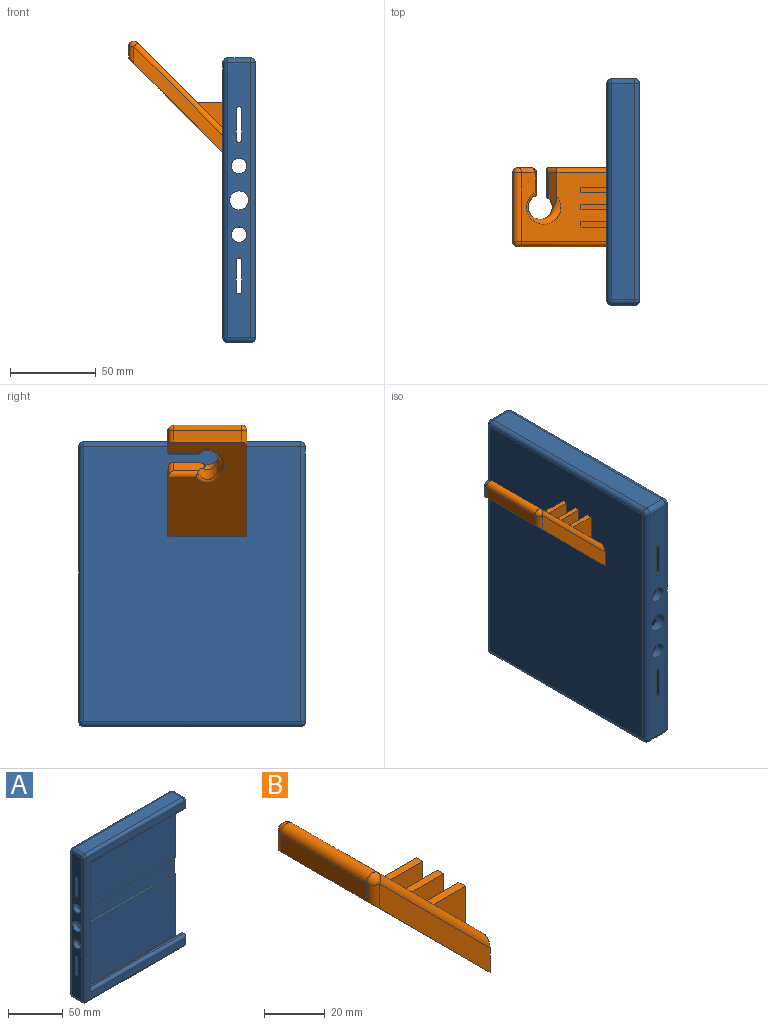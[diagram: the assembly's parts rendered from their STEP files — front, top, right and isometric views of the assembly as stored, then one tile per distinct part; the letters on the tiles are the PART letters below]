
ASSEMBLY  parts=2 mates=1
PART A: 63 faces, bbox 132x19x166 mm
  f0: plane 10x6.5mm, normal (1,0,0), area 25.9mm2, adj f23,f35,f36,f37,f54,f59
  f1: plane 71x6.5mm, normal (1,0,0), area 147.9mm2, adj f32,f33,f34,f35,f44,f54
  f2: plane 10x6.5mm, normal (1,0,0), area 25.9mm2, adj f24,f25,f26,f27,f53,f58
  f3: plane 40x11mm, normal (1,0,0), area 241.6mm2, adj f16,f17,f18,f25,f29,f30,f31,f32
  f4: plane 60x9mm, normal (1,0,0), area 435.4mm2, adj f6,f7,f8,f17,f20,f33,f34,f35
  f5: plane 60x9mm, normal (1,0,0), area 435.4mm2, adj f9,f10,f11,f15,f18,f25,f26,f27
  f6: cylinder r=1.5mm len=5mm, axis (1,0,0), area 23.6mm2, adj f4,f7,f20,f21
  f7: plane 18x5mm, normal (0,1,0), area 90mm2, adj f4,f6,f8,f21
  f8: cylinder r=1.5mm len=5mm, axis (1,0,0), area 23.6mm2, adj f4,f7,f20,f21
  f9: cylinder r=1.5mm len=5mm, axis (1,0,0), area 23.6mm2, adj f5,f10,f15,f21
  f10: plane 18x5mm, normal (0,-1,0), area 90mm2, adj f5,f9,f11,f21
  f11: cylinder r=1.5mm len=5mm, axis (1,0,0), area 23.6mm2, adj f5,f10,f15,f21
  f12: plane 126x13mm, normal (0,0,1), area 1638mm2, adj f42,f43,f52,f53
  f13: plane 160x126mm, normal (0,-1,0), area 2348mm2, adj f47,f52,f55,f58,f59,f60,f61,f62
  f14: plane 126x13mm, normal (0,0,-1), area 1638mm2, adj f45,f46,f54,f55
  f15: plane 18x5mm, normal (0,1,0), area 90mm2, adj f5,f9,f11,f21
  f16: cylinder r=5.5mm len=11mm, axis (1,0,0), area 206.5mm2, adj f3,f21,f25,f36,f38
  f17: cylinder r=4.5mm len=9mm, axis (1,0,0), area 141.4mm2, adj f3,f4,f21
  f18: cylinder r=4.5mm len=9mm, axis (1,0,0), area 141.4mm2, adj f3,f5,f21
  f19: plane 160x126mm, normal (0,1,0), area 20160mm2, adj f39,f43,f44,f45
  f20: plane 18x5mm, normal (0,-1,0), area 90mm2, adj f4,f6,f8,f21
  f21: plane 160x13mm, normal (-1,0,0), area 1735.6mm2, adj f6,f7,f8,f9,f10,f11,f15,f16
  f22: plane 71x6.5mm, normal (1,0,0), area 147.9mm2, adj f27,f28,f29,f30,f44,f53
  f23: plane 122x2mm, normal (0,0,1), area 244mm2, adj f0,f36,f38,f61
  f24: plane 122x2mm, normal (0,0,-1), area 244mm2, adj f2,f25,f38,f60
  f25: plane 127x74.84mm, normal (0,1,0), area 1350.2mm2, adj f2,f3,f5,f16,f24,f26,f38
  f26: plane 127x2.5mm, normal (0,0,-1), area 317.5mm2, adj f2,f5,f25,f27
  f27: cylinder r=2mm len=127mm, axis (-1,0,0), area 798mm2, adj f2,f5,f22,f26,f28
  f28: plane 127x2.5mm, normal (0,0,-1), area 317.5mm2, adj f5,f22,f27,f29
  f29: plane 127x69mm, normal (0,-1,0), area 8763mm2, adj f3,f5,f22,f28,f30
  f30: plane 127x2mm, normal (0,0,-1), area 254mm2, adj f3,f22,f29,f31
  f31: plane 127x18mm, normal (0,-1,0), area 2286mm2, adj f3,f30,f32,f44
  f32: plane 127x2mm, normal (0,0,1), area 254mm2, adj f1,f3,f31,f33
  f33: plane 127x69mm, normal (0,-1,0), area 8763mm2, adj f1,f3,f4,f32,f34
  f34: plane 127x2.5mm, normal (0,0,1), area 317.5mm2, adj f1,f4,f33,f35
  f35: cylinder r=2mm len=127mm, axis (-1,0,0), area 798mm2, adj f0,f1,f4,f34,f37
  f36: plane 127x74.84mm, normal (0,1,0), area 1350.2mm2, adj f0,f3,f4,f16,f23,f37,f38
  f37: plane 127x2.5mm, normal (0,0,1), area 317.5mm2, adj f0,f4,f35,f36
  f38: plane 140x2mm, normal (1,0,0), area 275.7mm2, adj f16,f23,f24,f25,f36,f62
  f39: cylinder r=3mm len=160mm, axis (0,0,-1), area 754mm2, adj f19,f21,f40,f41
  f40: sphere r=3mm, area 14.1mm2, adj f39,f42,f43
  f41: sphere r=3mm, area 14.1mm2, adj f39,f45,f46
  f42: cylinder r=3mm len=13mm, axis (0,1,0), area 61.3mm2, adj f12,f21,f40,f48
  f43: cylinder r=3mm len=126mm, axis (1,0,0), area 593.8mm2, adj f12,f19,f40,f49
  f44: cylinder r=3mm len=160mm, axis (0,0,1), area 754mm2, adj f1,f19,f22,f31,f49,f50
  f45: cylinder r=3mm len=126mm, axis (-1,0,0), area 593.8mm2, adj f14,f19,f41,f50
  f46: cylinder r=3mm len=13mm, axis (0,-1,0), area 61.3mm2, adj f14,f21,f41,f51
  f47: cylinder r=3mm len=160mm, axis (0,0,1), area 754mm2, adj f13,f21,f48,f51
  f48: sphere r=3mm, area 14.1mm2, adj f42,f47,f52
  f49: sphere r=3mm, area 14.1mm2, adj f43,f44,f53
  f50: sphere r=3mm, area 14.1mm2, adj f44,f45,f54
  f51: sphere r=3mm, area 14.1mm2, adj f46,f47,f55
  f52: cylinder r=3mm len=126mm, axis (-1,0,0), area 593.8mm2, adj f12,f13,f48,f56
  f53: cylinder r=3mm len=13mm, axis (0,-1,0), area 61.3mm2, adj f2,f12,f22,f49,f56
  f54: cylinder r=3mm len=13mm, axis (0,1,0), area 61.3mm2, adj f0,f1,f14,f50,f57
  f55: cylinder r=3mm len=126mm, axis (1,0,0), area 593.8mm2, adj f13,f14,f51,f57
  f56: sphere r=3mm, area 14.1mm2, adj f52,f53,f58
  f57: sphere r=3mm, area 14.1mm2, adj f54,f55,f59
  f58: cylinder r=3mm len=10mm, axis (0,0,-1), area 42mm2, adj f2,f13,f56,f60
  f59: cylinder r=3mm len=10mm, axis (0,0,-1), area 42mm2, adj f0,f13,f57,f61
  f60: cylinder r=3mm len=125mm, axis (1,0,0), area 574.9mm2, adj f13,f24,f58,f62
  f61: cylinder r=3mm len=125mm, axis (1,0,0), area 574.9mm2, adj f13,f23,f59,f62
  f62: cylinder r=3mm len=146mm, axis (0,0,-1), area 670mm2, adj f13,f38,f60,f61
PART B: 35 faces, bbox 58.2x47.3x66 mm
  f0: plane 49.7x49.7mm, normal (0.71,0,0.71), area 1981mm2, adj f3,f9,f10,f13,f15,f17,f18,f25
  f1: plane 38.89x33.94mm, normal (0,1,0), area 311.5mm2, adj f3,f4,f24,f25
  f2: plane 40x6.9mm, normal (-1,0,0), area 276mm2, adj f4,f11,f13,f14
  f3: plane 47.26x30.4mm, normal (1,0,0), area 780.1mm2, adj f0,f1,f4,f6,f10,f25,f26,f27
  f4: plane 56.08x56.08mm, normal (-0.71,0,-0.71), area 2821.9mm2, adj f1,f2,f3,f5,f6,f11,f14,f21
  f5: plane 12.93x7.98mm, normal (0,1,0), area 54.5mm2, adj f4,f14,f18,f20
  f6: plane 61.72x51.82mm, normal (0,-1,0), area 513mm2, adj f3,f4,f10,f11
  f7: cylinder r=7mm len=25.77mm, axis (0,0,-1), area 193.6mm2, adj f8,f9,f15,f17,f22,f23
  f8: plane 15.39x2.96mm, normal (0.71,0,-0.71), area 58mm2, adj f7,f17,f20,f21,f22
  f9: plane 18.79x5.14mm, normal (-0.71,0,0.71), area 119.6mm2, adj f0,f7,f15,f23,f24
  f10: cylinder r=3mm len=53.94mm, axis (0.71,0,-0.71), area 338.3mm2, adj f0,f3,f6,f12
  f11: cylinder r=3mm len=9.9mm, axis (0,0,1), area 39.6mm2, adj f2,f4,f6,f12
  f12: sphere r=3mm, area 21.2mm2, adj f10,f11,f13
  f13: cylinder r=3mm len=40mm, axis (0,1,0), area 282.7mm2, adj f0,f2,f12,f16
  f14: cylinder r=3mm len=9.9mm, axis (0,0,-1), area 39.6mm2, adj f2,f4,f5,f16
  f15: bspline ~22.11x19.99mm, area 207.8mm2, adj f0,f7,f9,f17
  f16: sphere r=3mm, area 23mm2, adj f13,f14,f18
  f17: cylinder r=3mm len=13.63mm, axis (0,1,0), area 59.3mm2, adj f0,f7,f8,f15,f19
  f18: cylinder r=3mm len=10.1mm, axis (0.71,0,-0.71), area 53.2mm2, adj f0,f5,f16,f19
  f19: sphere r=3mm, area 10.5mm2, adj f17,f18,f20
  f20: cylinder r=3mm len=7.07mm, axis (-0.71,0,-0.71), area 25.9mm2, adj f5,f8,f19,f21
  f21: cylinder r=3mm len=18.26mm, axis (0,-1,0), area 75.6mm2, adj f4,f8,f20,f22
  f22: bspline ~22.11x19.99mm, area 215.6mm2, adj f4,f7,f8,f21,f23
  f23: cylinder r=3mm len=17.98mm, axis (0,1,0), area 72.6mm2, adj f4,f7,f9,f22,f24
  f24: cylinder r=3mm len=9.19mm, axis (-0.71,0,-0.71), area 33mm2, adj f1,f9,f23,f25
  f25: cylinder r=3mm len=33.23mm, axis (0.71,0,-0.71), area 193.2mm2, adj f0,f1,f3,f24
  f26: plane 15x15mm, normal (0,1,0), area 112.5mm2, adj f0,f3,f28
  f27: plane 15x15mm, normal (0,-1,0), area 112.5mm2, adj f0,f3,f28
  f28: plane 15x3mm, normal (0,0,1), area 45mm2, adj f0,f3,f26,f27
  f29: plane 15x15mm, normal (0,1,0), area 112.5mm2, adj f0,f3,f31
  f30: plane 15x15mm, normal (0,-1,0), area 112.5mm2, adj f0,f3,f31
  f31: plane 15x3mm, normal (0,0,1), area 45mm2, adj f0,f3,f29,f30
  f32: plane 15x15mm, normal (0,1,0), area 112.5mm2, adj f0,f3,f34
  f33: plane 15x15mm, normal (0,-1,0), area 112.5mm2, adj f0,f3,f34
  f34: plane 15x3mm, normal (0,0,1), area 45mm2, adj f0,f3,f32,f33
PLACE A rot(axis=(0,0,1),90deg) t=(136.27,-21.1,-43.12)mm
PLACE B t=(67.45,30.9,-31.23)mm
MATE fastened A.f19 <-> B.f3  axis (1,0,0) through (122.27,30.9,-93.12)mm
